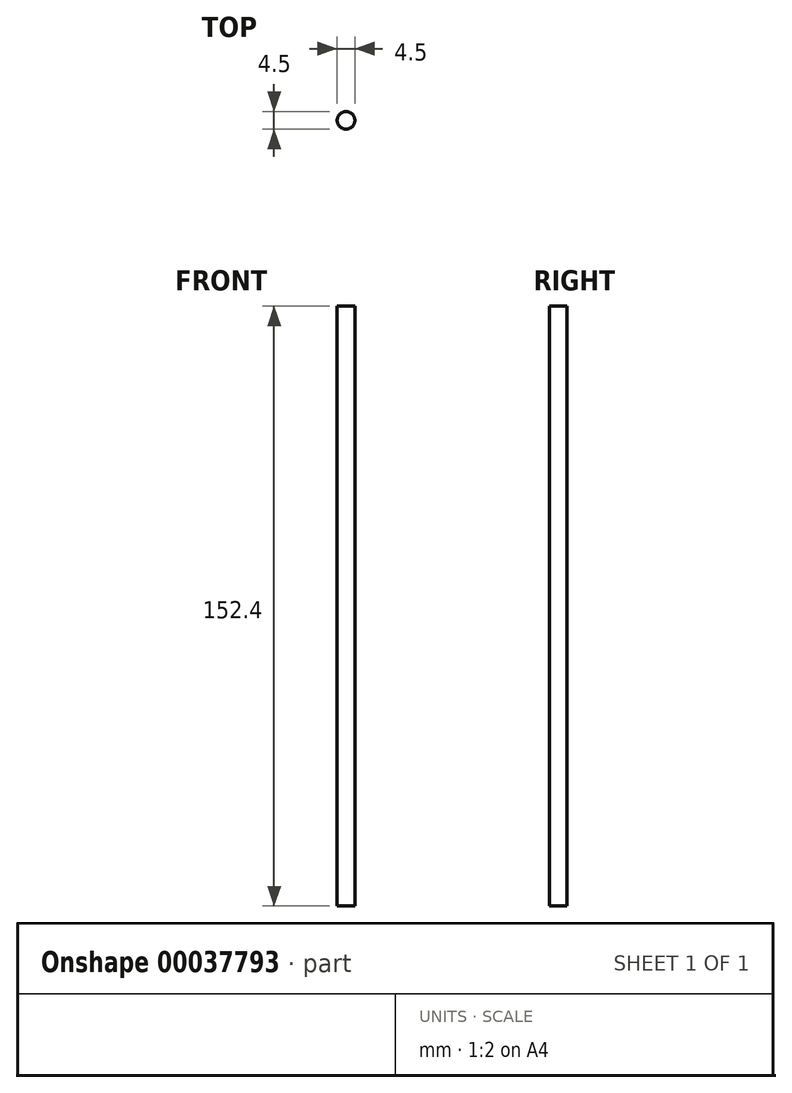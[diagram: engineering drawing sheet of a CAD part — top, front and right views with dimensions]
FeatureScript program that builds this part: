
annotation { "Feature Type Name" : "Feature", "Feature Type Description" : "" }
export const myFeature = defineFeature(function(context is Context, id is Id, definition is map)
    precondition{}
    {
        {
            var Q0;
            Q0=qCreatedBy(makeId("Top.planeOp"),FACE);
            var sketch = newSketch(context, id + "F0", { "sketchPlane" : qUnion([Q0])});
            skCircle(sketch, "E0", {"center": v(0, 0) * mm, "radius": 2.25 * mm});
            skSolve(sketch);
        }
        {
            var Q0;
            Q0 = qSketchRegion(id + "F0", true);
            extrude(context, id + "F1", {"entities" : qUnion([Q0]), "depth" : 152.4 * mm});
        }
    });
